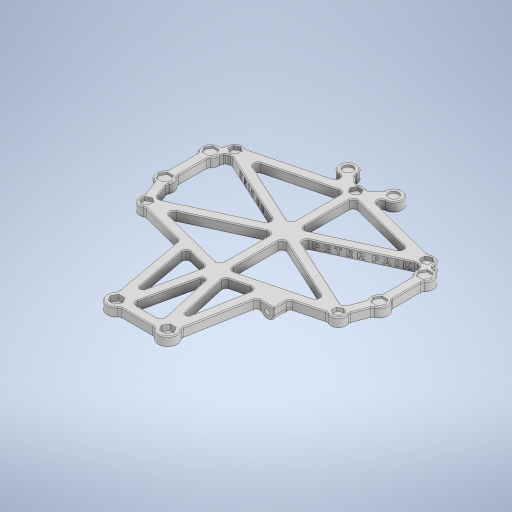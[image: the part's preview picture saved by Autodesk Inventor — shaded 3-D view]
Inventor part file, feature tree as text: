
AUTODESK INVENTOR PART (.ipt)
format: ipt  version: 2024.2 (Build 282272000, 272)  size: 1,593,856 bytes
history: native  units: in
note: dims shown in document units (in); Inventor stores cm internally (conversion verified against a paired STEP export)
features: extrude x11, sketch x10, fillet x3, hole x2, emboss x2, projected_geometry x1
ambient origin geometry x8: Origin, YZ Plane, XZ Plane, XY Plane, X Axis, Y Axis, Z Axis, Center Point
bodies: Solid1 (feature_tree)
feature tree (29):
  sketch  "Sketch1"  dims[d1=0.122in d2=1.9291in]
  extrude  "Extrusion1"  Depth=1.9291in
  sketch  "Sketch2"  dims[d3=2.4409in d5=0.2067in]
  extrude  "Extrusion2"  Depth=0.2067in
  extrude  "Extrusion3"  Depth=0.3937in
  sketch  "Sketch4"  dims[d6=0.2067in d7=0.3937in]
  extrude  "Extrusion4"  Depth=3.9764in
  extrude  "Extrusion10"  Depth=0.1969in
  hole  "Hole2"  [1 undecoded]
  extrude  "Extrusion6"  Depth=0.0984in
  sketch  "Sketch5"  dims[d13=0.5118in d14=3.9764in]
  hole  "Hole1"  [1 undecoded]
  extrude  "Extrusion12"  Depth=0.1969in
  extrude  "Extrusion5"  Depth=0.0098in
  fillet  "Fillet1"  Radius=0.1969in
  fillet  "Fillet2"  Radius=0.0984in
  fillet  "Fillet3"  Radius=0.0984in
  extrude  "Extrusion7"  Depth=0.0098in
  extrude  "Extrusion8"  Depth=0.0098in
  extrude  "Extrusion9"  Depth=0.0098in
  sketch  "Sketch10"  dims[d22=0.0984in d23=0.0984in]
  sketch  "Sketch11"  dims[d24=0.0984in d25=0.1969in]
  emboss  "Emboss1"
  emboss  "Emboss2"
  projected_geometry  "Projected Loop1"
  sketch  "Sketch6"  dims[d15=1.9882in d17=0.1969in]
  sketch  "Sketch7"  dims[d18=0.1969in d19=0.1969in]
  sketch  "Sketch8"  dims[d20=0.0984in d21=0.0984in]
  sketch  "Sketch14"  dims[d26=0.0984in d27=0.0984in d30=0.1969in d31=0.0984in d32=0.0984in d35=0.2244in d36=0.9449in d37=0.315in d38=0.1929in d39=2.9528in d40=0.6063in d41=0.1969in d42=0.1969in d43=0.0984in d44=0.0984in d48=1.2598in d49=1.063in d51=0.2362in d52=0.2362in d53=0.1969in d55=0.1969in d56=0.1969in d57=0.1969in d66=0.3543in d67=0.1969in d68=0.0984in d69=0.1969in d70=0.0984in d71=0.0984in d72=0.1969in d73=0.0984in d74=0.0984in d75=0.1969in d76=0.0984in d77=0.0984in d78=0.1969in d79=0.0984in d80=0.1969in d81=0.0984in d82=0.3937in d83=0.1969in d84=0.0984in d85=1.5748in d86=0.0984in d87=0.0984in d88=0.1969in d89=0.0in d90=0.4466in d91=0.4466in d92=0.9449in d93=0.3543in d94=0.0984in d95=0.4724in d96=0.315in d97=0.0984in d100=0.0984in d101=0.0984in d102=0.1969in d103=0.0in d104=0.0748in d105=0.0in d106=0.0394in d107=0.0in d108=0.1083in d110=0.315in d111=0.0in d112=0.2067in d113=0.1339in d114=0.2362in d115=0.1575in d116=0.0787in d117=90.0deg d118=0.0787in d119=0.8108in d120=0.0394in d121=0.0in d122=0.1181in d123=0.0in d124=0.0787in d125=0.0787in d127=0.0197in d128=0.0984in d129=0.7874in d130=0.1378in d131=0.1083in d132=0.2362in d133=0.1575in d134=0.0787in d135=90.0deg d136=0.2362in d137=0.0in d138=0.0079in d139=0.0in d140=0.0079in d141=0.0in d142=0.0079in d143=0.0in d144=0.1378in d145=0.1378in d146=0.0079in d147=0.0in d148=0.0098in d149=0.0in d150=0.0098in d151=0.0in d154=0.0492in d155=0.2067in d156=0.0394in d157=0.0in]
note: 2 required parameter values undecoded (feature->parameter linkage not recoverable at this tier; creation-order binding heuristic only, values carry confidence <= 0.55)
